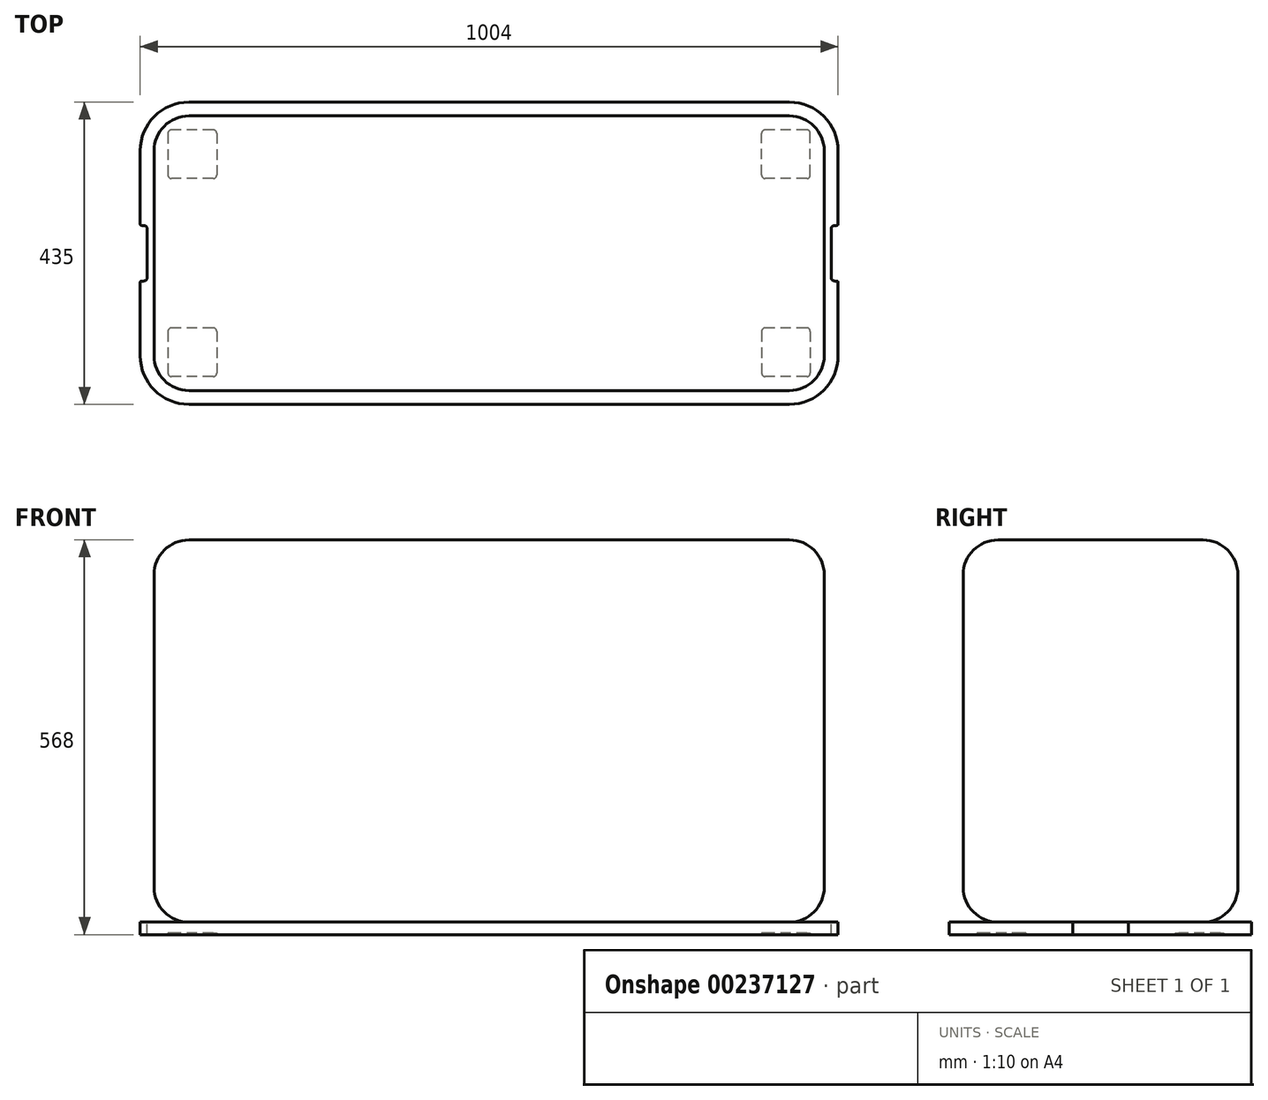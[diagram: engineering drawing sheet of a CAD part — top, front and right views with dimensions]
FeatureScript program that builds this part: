
annotation { "Feature Type Name" : "Feature", "Feature Type Description" : "" }
export const myFeature = defineFeature(function(context is Context, id is Id, definition is map)
    precondition{}
    {
        {
            var Q0;
            Q0=qCreatedBy(makeId("Top.planeOp"),FACE);
            var sketch = newSketch(context, id + "F0", { "sketchPlane" : qUnion([Q0])});
            skLineSegment(sketch, "E0.bottom", {"start": v(502, -217.5) * mm, "end": v(-502, -217.5) * mm});
            skLineSegment(sketch, "E0.top", {"start": v(502, 217.5) * mm, "end": v(-502, 217.5) * mm});
            skLineSegment(sketch, "E0.left", {"start": v(502, -217.5) * mm, "end": v(502, 217.5) * mm});
            skLineSegment(sketch, "E0.right", {"start": v(-502, -217.5) * mm, "end": v(-502, 217.5) * mm});
            skPoint(sketch, "E0.middle", {"position": v(0, 0) * mm});
            skSolve(sketch);
        }
        {
            var Q0;
            Q0 = qSketchRegion(id + "F0", true);
            extrude(context, id + "F1", {"entities" : qUnion([Q0]), "depth" : 18 * mm});
        }
        {
            var Q0;
            Q0=makeQuery(id+"F1.opExtrude","SWEPT_EDGE",EDGE,{"disambiguationData":[OSD([sQuery(id+"F0.wireOp",EDGE,"E0.bottom"),sQuery(id+"F0.wireOp",EDGE,"E0.right")])]});
            var Q1;
            Q1=makeQuery(id+"F1.opExtrude","SWEPT_EDGE",EDGE,{"disambiguationData":[OSD([sQuery(id+"F0.wireOp",EDGE,"E0.top"),sQuery(id+"F0.wireOp",EDGE,"E0.right")])]});
            var Q2;
            Q2=makeQuery(id+"F1.opExtrude","SWEPT_EDGE",EDGE,{"disambiguationData":[OSD([sQuery(id+"F0.wireOp",EDGE,"E0.top"),sQuery(id+"F0.wireOp",EDGE,"E0.left")])]});
            var Q3;
            Q3=makeQuery(id+"F1.opExtrude","SWEPT_EDGE",EDGE,{"disambiguationData":[OSD([sQuery(id+"F0.wireOp",EDGE,"E0.bottom"),sQuery(id+"F0.wireOp",EDGE,"E0.left")])]});
            fillet(context, id + "F2", {"entities" : qUnion([Q0, Q1, Q2, Q3]), "radius" : 70 * mm, "tangentPropagation" : true, "allowEdgeOverflow" : false});
        }
        {
            var Q0;
            Q0=makeQuery(id+"F1.opExtrude","CAP_FACE",FACE,{"disambiguationData":[OSD([sQuery(id+"F0.wireOp",EDGE,"E0.bottom"),sQuery(id+"F0.wireOp",EDGE,"E0.top"),sQuery(id+"F0.wireOp",EDGE,"E0.left"),sQuery(id+"F0.wireOp",EDGE,"E0.right")])],"isStart":true});
            var sketch = newSketch(context, id + "F3", { "sketchPlane" : qUnion([Q0])});
            skLineSegment(sketch, "E1.bottom", {"start": v(-392, 107.5) * mm, "end": v(-462, 107.5) * mm});
            skLineSegment(sketch, "E1.top", {"start": v(-392, 177.5) * mm, "end": v(-462, 177.5) * mm});
            skLineSegment(sketch, "E1.left", {"start": v(-392, 107.5) * mm, "end": v(-392, 177.5) * mm});
            skLineSegment(sketch, "E1.right", {"start": v(-462, 107.5) * mm, "end": v(-462, 177.5) * mm});
            skPoint(sketch, "E1.middle", {"position": v(-427, 142.5) * mm});
            skLineSegment(sketch, "E2.bottom", {"start": v(-392, -177.5) * mm, "end": v(-462, -177.5) * mm});
            skLineSegment(sketch, "E2.top", {"start": v(-392, -107.5) * mm, "end": v(-462, -107.5) * mm});
            skLineSegment(sketch, "E2.left", {"start": v(-392, -177.5) * mm, "end": v(-392, -107.5) * mm});
            skLineSegment(sketch, "E2.right", {"start": v(-462, -177.5) * mm, "end": v(-462, -107.5) * mm});
            skPoint(sketch, "E2.middle", {"position": v(-427, -142.5) * mm});
            skLineSegment(sketch, "E3.bottom", {"start": v(462, -107.5) * mm, "end": v(392, -107.5) * mm});
            skLineSegment(sketch, "E3.top", {"start": v(462, -177.5) * mm, "end": v(392, -177.5) * mm});
            skLineSegment(sketch, "E3.left", {"start": v(462, -107.5) * mm, "end": v(462, -177.5) * mm});
            skLineSegment(sketch, "E3.right", {"start": v(392, -107.5) * mm, "end": v(392, -177.5) * mm});
            skPoint(sketch, "E3.middle", {"position": v(427, -142.5) * mm});
            skLineSegment(sketch, "E4.bottom", {"start": v(462, 107.5) * mm, "end": v(392, 107.5) * mm});
            skLineSegment(sketch, "E4.top", {"start": v(462, 177.5) * mm, "end": v(392, 177.5) * mm});
            skLineSegment(sketch, "E4.left", {"start": v(462, 107.5) * mm, "end": v(462, 177.5) * mm});
            skLineSegment(sketch, "E4.right", {"start": v(392, 107.5) * mm, "end": v(392, 177.5) * mm});
            skPoint(sketch, "E4.middle", {"position": v(427, 142.5) * mm});
            skSolve(sketch);
        }
        {
            var Q0;
            Q0 = qSketchRegion(id + "F3", true);
            extrude(context, id + "F4", {"entities" : qUnion([Q0]), "operationType" : NewBodyOperationType.REMOVE, "oppositeDirection" : true, "depth" : 2 * mm});
        }
        {
            var Q0;
            Q0=makeQuery(id+"F4.boolean.opBoolean","COPY",EDGE,{"derivedFrom":makeQuery(id+"F4.opExtrude","SWEPT_EDGE",EDGE,{"disambiguationData":[OSD([sQuery(id+"F3.wireOp",EDGE,"E1.top"),sQuery(id+"F3.wireOp",EDGE,"E1.right")])]})});
            var Q1;
            Q1=makeQuery(id+"F4.boolean.opBoolean","COPY",EDGE,{"derivedFrom":makeQuery(id+"F4.opExtrude","SWEPT_EDGE",EDGE,{"disambiguationData":[OSD([sQuery(id+"F3.wireOp",EDGE,"E1.top"),sQuery(id+"F3.wireOp",EDGE,"E1.left")])]})});
            var Q2;
            Q2=makeQuery(id+"F4.boolean.opBoolean","COPY",EDGE,{"derivedFrom":makeQuery(id+"F4.opExtrude","SWEPT_EDGE",EDGE,{"disambiguationData":[OSD([sQuery(id+"F3.wireOp",EDGE,"E1.bottom"),sQuery(id+"F3.wireOp",EDGE,"E1.right")])]})});
            var Q3;
            Q3=makeQuery(id+"F4.boolean.opBoolean","COPY",EDGE,{"derivedFrom":makeQuery(id+"F4.opExtrude","SWEPT_EDGE",EDGE,{"disambiguationData":[OSD([sQuery(id+"F3.wireOp",EDGE,"E1.bottom"),sQuery(id+"F3.wireOp",EDGE,"E1.left")])]})});
            var Q4;
            Q4=makeQuery(id+"F4.boolean.opBoolean","COPY",EDGE,{"derivedFrom":makeQuery(id+"F4.opExtrude","SWEPT_EDGE",EDGE,{"disambiguationData":[OSD([sQuery(id+"F3.wireOp",EDGE,"E2.bottom"),sQuery(id+"F3.wireOp",EDGE,"E2.left")])]})});
            var Q5;
            Q5=makeQuery(id+"F4.boolean.opBoolean","COPY",EDGE,{"derivedFrom":makeQuery(id+"F4.opExtrude","SWEPT_EDGE",EDGE,{"disambiguationData":[OSD([sQuery(id+"F3.wireOp",EDGE,"E2.bottom"),sQuery(id+"F3.wireOp",EDGE,"E2.right")])]})});
            var Q6;
            Q6=makeQuery(id+"F4.boolean.opBoolean","COPY",EDGE,{"derivedFrom":makeQuery(id+"F4.opExtrude","SWEPT_EDGE",EDGE,{"disambiguationData":[OSD([sQuery(id+"F3.wireOp",EDGE,"E2.top"),sQuery(id+"F3.wireOp",EDGE,"E2.left")])]})});
            var Q7;
            Q7=makeQuery(id+"F4.boolean.opBoolean","COPY",EDGE,{"derivedFrom":makeQuery(id+"F4.opExtrude","SWEPT_EDGE",EDGE,{"disambiguationData":[OSD([sQuery(id+"F3.wireOp",EDGE,"E2.top"),sQuery(id+"F3.wireOp",EDGE,"E2.right")])]})});
            var Q8;
            Q8=makeQuery(id+"F4.boolean.opBoolean","COPY",EDGE,{"derivedFrom":makeQuery(id+"F4.opExtrude","SWEPT_EDGE",EDGE,{"disambiguationData":[OSD([sQuery(id+"F3.wireOp",EDGE,"E3.bottom"),sQuery(id+"F3.wireOp",EDGE,"E3.right")])]})});
            var Q9;
            Q9=makeQuery(id+"F4.boolean.opBoolean","COPY",EDGE,{"derivedFrom":makeQuery(id+"F4.opExtrude","SWEPT_EDGE",EDGE,{"disambiguationData":[OSD([sQuery(id+"F3.wireOp",EDGE,"E3.bottom"),sQuery(id+"F3.wireOp",EDGE,"E3.left")])]})});
            var Q10;
            Q10=makeQuery(id+"F4.boolean.opBoolean","COPY",EDGE,{"derivedFrom":makeQuery(id+"F4.opExtrude","SWEPT_EDGE",EDGE,{"disambiguationData":[OSD([sQuery(id+"F3.wireOp",EDGE,"E3.top"),sQuery(id+"F3.wireOp",EDGE,"E3.right")])]})});
            var Q11;
            Q11=makeQuery(id+"F4.boolean.opBoolean","COPY",EDGE,{"derivedFrom":makeQuery(id+"F4.opExtrude","SWEPT_EDGE",EDGE,{"disambiguationData":[OSD([sQuery(id+"F3.wireOp",EDGE,"E3.top"),sQuery(id+"F3.wireOp",EDGE,"E3.left")])]})});
            var Q12;
            Q12=makeQuery(id+"F4.boolean.opBoolean","COPY",EDGE,{"derivedFrom":makeQuery(id+"F4.opExtrude","SWEPT_EDGE",EDGE,{"disambiguationData":[OSD([sQuery(id+"F3.wireOp",EDGE,"E4.bottom"),sQuery(id+"F3.wireOp",EDGE,"E4.left")])]})});
            var Q13;
            Q13=makeQuery(id+"F4.boolean.opBoolean","COPY",EDGE,{"derivedFrom":makeQuery(id+"F4.opExtrude","SWEPT_EDGE",EDGE,{"disambiguationData":[OSD([sQuery(id+"F3.wireOp",EDGE,"E4.bottom"),sQuery(id+"F3.wireOp",EDGE,"E4.right")])]})});
            var Q14;
            Q14=makeQuery(id+"F4.boolean.opBoolean","COPY",EDGE,{"derivedFrom":makeQuery(id+"F4.opExtrude","SWEPT_EDGE",EDGE,{"disambiguationData":[OSD([sQuery(id+"F3.wireOp",EDGE,"E4.top"),sQuery(id+"F3.wireOp",EDGE,"E4.left")])]})});
            var Q15;
            Q15=makeQuery(id+"F4.boolean.opBoolean","COPY",EDGE,{"derivedFrom":makeQuery(id+"F4.opExtrude","SWEPT_EDGE",EDGE,{"disambiguationData":[OSD([sQuery(id+"F3.wireOp",EDGE,"E4.top"),sQuery(id+"F3.wireOp",EDGE,"E4.right")])]})});
            fillet(context, id + "F5", {"entities" : qUnion([Q0, Q1, Q2, Q3, Q4, Q5, Q6, Q7, Q8, Q9, Q10, Q11, Q12, Q13, Q14, Q15]), "radius" : 5 * mm, "tangentPropagation" : true, "allowEdgeOverflow" : false});
        }
        {
            var Q0;
            Q0=makeQuery(id+"F1.opExtrude","CAP_FACE",FACE,{"disambiguationData":[OSD([sQuery(id+"F0.wireOp",EDGE,"E0.bottom"),sQuery(id+"F0.wireOp",EDGE,"E0.top"),sQuery(id+"F0.wireOp",EDGE,"E0.left"),sQuery(id+"F0.wireOp",EDGE,"E0.right")])],"isStart":false});
            var sketch = newSketch(context, id + "F6", { "sketchPlane" : qUnion([Q0])});
            skLineSegment(sketch, "E5.bottom", {"start": v(-512, -40) * mm, "end": v(-492, -40) * mm});
            skLineSegment(sketch, "E5.top", {"start": v(-512, 40) * mm, "end": v(-492, 40) * mm});
            skLineSegment(sketch, "E5.left", {"start": v(-512, -40) * mm, "end": v(-512, 40) * mm});
            skLineSegment(sketch, "E5.right", {"start": v(-492, -40) * mm, "end": v(-492, 40) * mm});
            skPoint(sketch, "E5.middle", {"position": v(-502, 0) * mm});
            skLineSegment(sketch, "E6.bottom", {"start": v(512, -40) * mm, "end": v(492, -40) * mm});
            skLineSegment(sketch, "E6.top", {"start": v(512, 40) * mm, "end": v(492, 40) * mm});
            skLineSegment(sketch, "E6.left", {"start": v(512, -40) * mm, "end": v(512, 40) * mm});
            skLineSegment(sketch, "E6.right", {"start": v(492, -40) * mm, "end": v(492, 40) * mm});
            skPoint(sketch, "E6.middle", {"position": v(502, 0) * mm});
            skLineSegment(sketch, "E7", {"start": v(-502, 0) * mm, "end": v(502, 0) * mm, "construction": true});
            skSolve(sketch);
        }
        {
            var Q0;
            Q0 = qSketchRegion(id + "F6", true);
            extrude(context, id + "F7", {"entities" : qUnion([Q0]), "operationType" : NewBodyOperationType.REMOVE, "oppositeDirection" : true, "depth" : 18 * mm});
        }
        {
            var Q0;
            Q0=makeQuery(id+"F7.boolean.opBoolean","COPY",EDGE,{"derivedFrom":makeQuery(id+"F7.opExtrude","SWEPT_EDGE",EDGE,{"disambiguationData":[OSD([sQuery(id+"F6.wireOp",EDGE,"E5.top"),sQuery(id+"F6.wireOp",EDGE,"E5.left")])]})});
            var Q1;
            Q1=makeQuery(id+"F7.boolean.opBoolean","COPY",EDGE,{"derivedFrom":makeQuery(id+"F7.opExtrude","SWEPT_EDGE",EDGE,{"disambiguationData":[OSD([sQuery(id+"F6.wireOp",EDGE,"E5.top"),sQuery(id+"F6.wireOp",EDGE,"E5.right")])]})});
            var Q2;
            Q2=makeQuery(id+"F7.boolean.opBoolean","COPY",EDGE,{"derivedFrom":makeQuery(id+"F7.opExtrude","SWEPT_EDGE",EDGE,{"disambiguationData":[OSD([sQuery(id+"F6.wireOp",EDGE,"E5.bottom"),sQuery(id+"F6.wireOp",EDGE,"E5.left")])]})});
            var Q3;
            Q3=makeQuery(id+"F7.boolean.opBoolean","COPY",EDGE,{"derivedFrom":makeQuery(id+"F7.opExtrude","SWEPT_EDGE",EDGE,{"disambiguationData":[OSD([sQuery(id+"F6.wireOp",EDGE,"E5.bottom"),sQuery(id+"F6.wireOp",EDGE,"E5.right")])]})});
            var Q4;
            Q4=makeQuery(id+"F7.boolean.opBoolean","COPY",EDGE,{"derivedFrom":makeQuery(id+"F7.opExtrude","SWEPT_EDGE",EDGE,{"disambiguationData":[OSD([sQuery(id+"F6.wireOp",EDGE,"E6.bottom"),sQuery(id+"F6.wireOp",EDGE,"E6.left")])]})});
            var Q5;
            Q5=makeQuery(id+"F7.boolean.opBoolean","COPY",EDGE,{"derivedFrom":makeQuery(id+"F7.opExtrude","SWEPT_EDGE",EDGE,{"disambiguationData":[OSD([sQuery(id+"F6.wireOp",EDGE,"E6.bottom"),sQuery(id+"F6.wireOp",EDGE,"E6.right")])]})});
            var Q6;
            Q6=makeQuery(id+"F7.boolean.opBoolean","COPY",EDGE,{"derivedFrom":makeQuery(id+"F7.opExtrude","SWEPT_EDGE",EDGE,{"disambiguationData":[OSD([sQuery(id+"F6.wireOp",EDGE,"E6.top"),sQuery(id+"F6.wireOp",EDGE,"E6.left")])]})});
            var Q7;
            Q7=makeQuery(id+"F7.boolean.opBoolean","COPY",EDGE,{"derivedFrom":makeQuery(id+"F7.opExtrude","SWEPT_EDGE",EDGE,{"disambiguationData":[OSD([sQuery(id+"F6.wireOp",EDGE,"E6.top"),sQuery(id+"F6.wireOp",EDGE,"E6.right")])]})});
            fillet(context, id + "F8", {"entities" : qUnion([Q0, Q1, Q2, Q3, Q4, Q5, Q6, Q7]), "radius" : 5 * mm, "tangentPropagation" : true, "allowEdgeOverflow" : false});
        }
        {
            var Q0;
            Q0=makeQuery(id+"F1.opExtrude","CAP_FACE",FACE,{"disambiguationData":[OSD([sQuery(id+"F0.wireOp",EDGE,"E0.bottom"),sQuery(id+"F0.wireOp",EDGE,"E0.top"),sQuery(id+"F0.wireOp",EDGE,"E0.left"),sQuery(id+"F0.wireOp",EDGE,"E0.right")])],"isStart":false});
            var sketch = newSketch(context, id + "F9", { "sketchPlane" : qUnion([Q0])});
            skLineSegment(sketch, "E8.bottom", {"start": v(482, -197.5) * mm, "end": v(-482, -197.5) * mm});
            skLineSegment(sketch, "E8.top", {"start": v(482, 197.5) * mm, "end": v(-482, 197.5) * mm});
            skLineSegment(sketch, "E8.left", {"start": v(482, -197.5) * mm, "end": v(482, 197.5) * mm});
            skLineSegment(sketch, "E8.right", {"start": v(-482, -197.5) * mm, "end": v(-482, 197.5) * mm});
            skPoint(sketch, "E8.middle", {"position": v(0, 0) * mm});
            skSolve(sketch);
        }
        {
            var Q0;
            Q0 = qSketchRegion(id + "F9", true);
            extrude(context, id + "F10", {"entities" : qUnion([Q0]), "depth" : 550 * mm});
        }
        {
            var Q0;
            Q0=makeQuery(id+"F10.opExtrude","CAP_EDGE",EDGE,{"disambiguationData":[OSD([sQuery(id+"F9.wireOp",EDGE,"E8.left")])],"isStart":false});
            var Q1;
            Q1=makeQuery(id+"F10.opExtrude","CAP_EDGE",EDGE,{"disambiguationData":[OSD([sQuery(id+"F9.wireOp",EDGE,"E8.right")])],"isStart":false});
            var Q2;
            Q2=makeQuery(id+"F10.opExtrude","CAP_EDGE",EDGE,{"disambiguationData":[OSD([sQuery(id+"F9.wireOp",EDGE,"E8.bottom")])],"isStart":false});
            var Q3;
            Q3=makeQuery(id+"F10.opExtrude","SWEPT_EDGE",EDGE,{"disambiguationData":[OSD([sQuery(id+"F9.wireOp",EDGE,"E8.bottom"),sQuery(id+"F9.wireOp",EDGE,"E8.left")])]});
            var Q4;
            Q4=makeQuery(id+"F10.opExtrude","SWEPT_EDGE",EDGE,{"disambiguationData":[OSD([sQuery(id+"F9.wireOp",EDGE,"E8.bottom"),sQuery(id+"F9.wireOp",EDGE,"E8.right")])]});
            var Q5;
            Q5=makeQuery(id+"F10.opExtrude","CAP_EDGE",EDGE,{"disambiguationData":[OSD([sQuery(id+"F9.wireOp",EDGE,"E8.bottom")])],"isStart":true});
            var Q6;
            Q6=makeQuery(id+"F10.opExtrude","CAP_EDGE",EDGE,{"disambiguationData":[OSD([sQuery(id+"F9.wireOp",EDGE,"E8.left")])],"isStart":true});
            var Q7;
            Q7=makeQuery(id+"F10.opExtrude","SWEPT_EDGE",EDGE,{"disambiguationData":[OSD([sQuery(id+"F9.wireOp",EDGE,"E8.top"),sQuery(id+"F9.wireOp",EDGE,"E8.left")])]});
            var Q8;
            Q8=makeQuery(id+"F10.opExtrude","CAP_EDGE",EDGE,{"disambiguationData":[OSD([sQuery(id+"F9.wireOp",EDGE,"E8.top")])],"isStart":false});
            var Q9;
            Q9=makeQuery(id+"F10.opExtrude","CAP_EDGE",EDGE,{"disambiguationData":[OSD([sQuery(id+"F9.wireOp",EDGE,"E8.top")])],"isStart":true});
            var Q10;
            Q10=makeQuery(id+"F10.opExtrude","SWEPT_EDGE",EDGE,{"disambiguationData":[OSD([sQuery(id+"F9.wireOp",EDGE,"E8.top"),sQuery(id+"F9.wireOp",EDGE,"E8.right")])]});
            var Q11;
            Q11=makeQuery(id+"F10.opExtrude","CAP_EDGE",EDGE,{"disambiguationData":[OSD([sQuery(id+"F9.wireOp",EDGE,"E8.right")])],"isStart":true});
            fillet(context, id + "F11", {"entities" : qUnion([Q0, Q1, Q2, Q3, Q4, Q5, Q6, Q7, Q8, Q9, Q10, Q11]), "radius" : 50 * mm, "tangentPropagation" : true, "allowEdgeOverflow" : false});
        }
        {
            var Q0;
            Q0=makeQuery(id+"F7.boolean.opBoolean","INTERSECT",EDGE,{"derivedFrom":[makeQuery(id+"F1.opExtrude","SWEPT_FACE",FACE,{"disambiguationData":[OSD([sQuery(id+"F0.wireOp",EDGE,"E0.right")])]}),makeQuery(id+"F7.opExtrude","SWEPT_FACE",FACE,{"disambiguationData":[OSD([sQuery(id+"F6.wireOp",EDGE,"E5.bottom")])]})]});
            var Q1;
            Q1=makeQuery(id+"F7.boolean.opBoolean","INTERSECT",EDGE,{"derivedFrom":[makeQuery(id+"F1.opExtrude","SWEPT_FACE",FACE,{"disambiguationData":[OSD([sQuery(id+"F0.wireOp",EDGE,"E0.right")])]}),makeQuery(id+"F7.opExtrude","SWEPT_FACE",FACE,{"disambiguationData":[OSD([sQuery(id+"F6.wireOp",EDGE,"E5.top")])]})]});
            var Q2;
            Q2=makeQuery(id+"F7.boolean.opBoolean","INTERSECT",EDGE,{"derivedFrom":[makeQuery(id+"F1.opExtrude","SWEPT_FACE",FACE,{"disambiguationData":[OSD([sQuery(id+"F0.wireOp",EDGE,"E0.left")])]}),makeQuery(id+"F7.opExtrude","SWEPT_FACE",FACE,{"disambiguationData":[OSD([sQuery(id+"F6.wireOp",EDGE,"E6.top")])]})]});
            var Q3;
            Q3=makeQuery(id+"F7.boolean.opBoolean","INTERSECT",EDGE,{"derivedFrom":[makeQuery(id+"F1.opExtrude","SWEPT_FACE",FACE,{"disambiguationData":[OSD([sQuery(id+"F0.wireOp",EDGE,"E0.left")])]}),makeQuery(id+"F7.opExtrude","SWEPT_FACE",FACE,{"disambiguationData":[OSD([sQuery(id+"F6.wireOp",EDGE,"E6.bottom")])]})]});
            fillet(context, id + "F12", {"entities" : qUnion([Q0, Q1, Q2, Q3]), "radius" : 2 * mm, "tangentPropagation" : true, "allowEdgeOverflow" : false});
        }
    });
